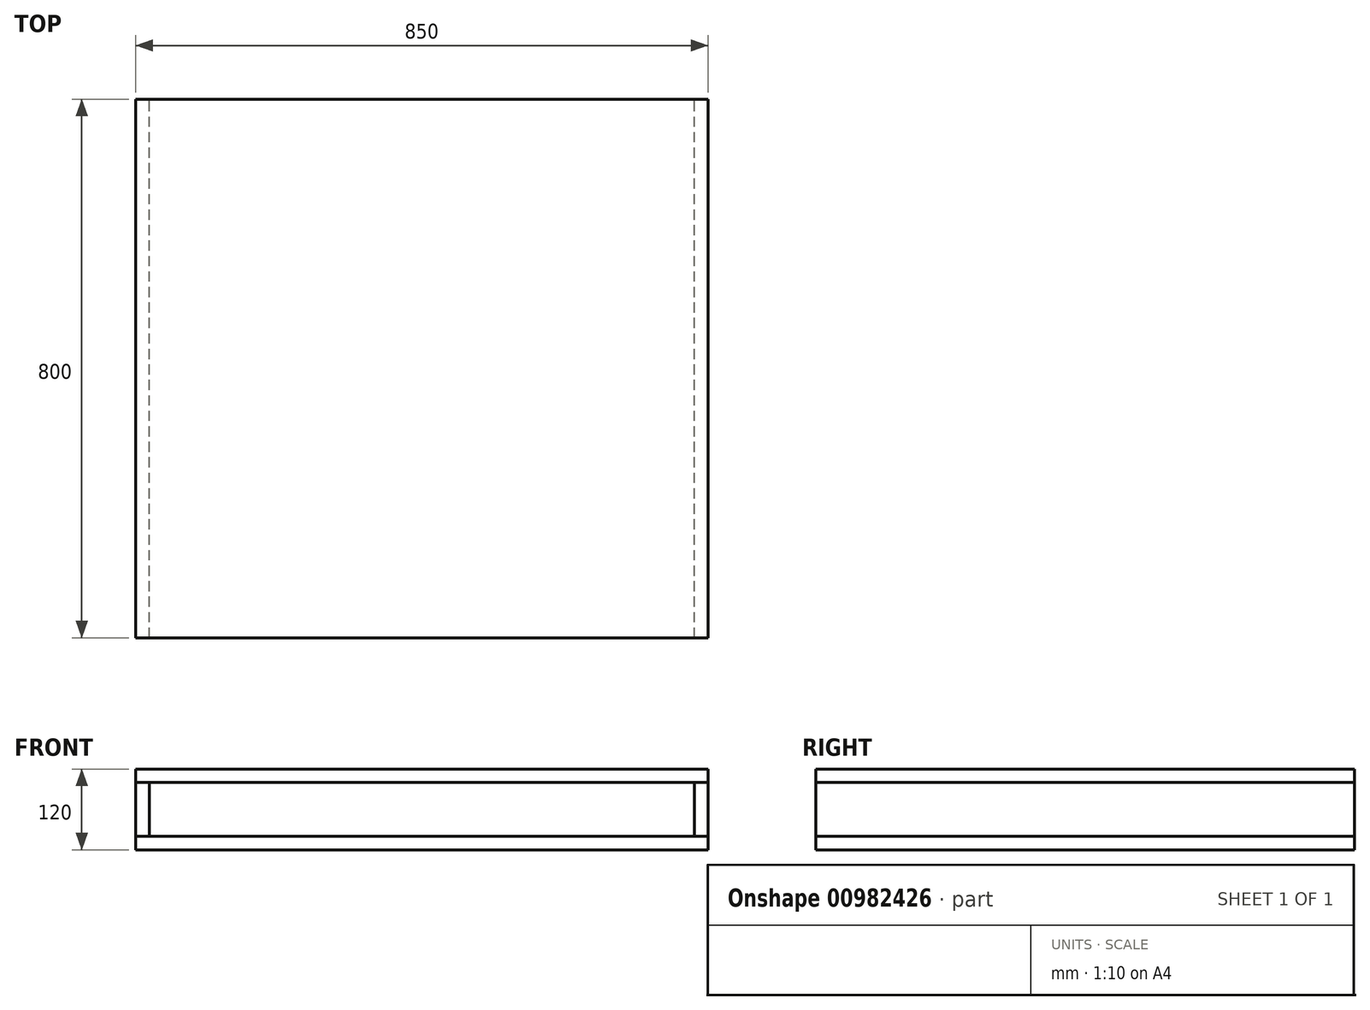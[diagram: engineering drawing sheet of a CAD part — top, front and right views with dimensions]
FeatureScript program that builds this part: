
annotation { "Feature Type Name" : "Feature", "Feature Type Description" : "" }
export const myFeature = defineFeature(function(context is Context, id is Id, definition is map)
    precondition{}
    {
        {
            var Q0;
            Q0=qCreatedBy(makeId("Front.planeOp"),FACE);
            var sketch = newSketch(context, id + "F0", { "sketchPlane" : qUnion([Q0])});
            skLineSegment(sketch, "E0.bottom", {"start": v(-425, 385) * mm, "end": v(425, 385) * mm});
            skLineSegment(sketch, "E0.top", {"start": v(-425, -385) * mm, "end": v(425, -385) * mm});
            skLineSegment(sketch, "E0.left", {"start": v(-425, 385) * mm, "end": v(-425, -385) * mm});
            skLineSegment(sketch, "E0.right", {"start": v(425, 385) * mm, "end": v(425, -385) * mm});
            skPoint(sketch, "E0.middle", {"position": v(0, 0) * mm});
            skLineSegment(sketch, "E1", {"start": v(-425, 365) * mm, "end": v(425, 365) * mm});
            skLineSegment(sketch, "E2", {"start": v(-425, 285) * mm, "end": v(425, 285) * mm});
            skLineSegment(sketch, "E3", {"start": v(-425, 265) * mm, "end": v(425, 265) * mm});
            skLineSegment(sketch, "E4", {"start": v(-405, 365) * mm, "end": v(-405, 285) * mm});
            skLineSegment(sketch, "E5", {"start": v(405, 365) * mm, "end": v(405, 285) * mm});
            skSolve(sketch);
        }
        {
            var Q0;
            {var subQ0=sQuery(id+"F0.wireOp",EDGE,"E0.bottom");Q0=makeQuery(id+"F0.imprint","IMPRINT",FACE,{"disambiguationData":[TD([[makeQuery(id+"F0.imprint","IMPRINT",EDGE,{"derivedFrom":subQ0}),-1.0]])]});}
            var Q1;
            {var subQ6=sQuery(id+"F0.wireOp",EDGE,"E3");Q1=makeQuery(id+"F0.imprint","IMPRINT",FACE,{"disambiguationData":[TD([[makeQuery(id+"F0.imprint","IMPRINT",EDGE,{"derivedFrom":subQ6}),1.0]])]});}
            extrude(context, id + "F1", {"entities" : qUnion([Q0, Q1]), "depth" : 800 * mm, "offsetDistance" : 25 * mm});
        }
        {
            var Q0;
            {var subQ5=sQuery(id+"F0.wireOp",EDGE,"E5");Q0=makeQuery(id+"F0.imprint","IMPRINT",FACE,{"disambiguationData":[TD([[makeQuery(id+"F0.imprint","IMPRINT",EDGE,{"derivedFrom":subQ5}),1.0]])]});}
            var Q1;
            {var subQ5=sQuery(id+"F0.wireOp",EDGE,"E4");Q1=makeQuery(id+"F0.imprint","IMPRINT",FACE,{"disambiguationData":[TD([[makeQuery(id+"F0.imprint","IMPRINT",EDGE,{"derivedFrom":subQ5}),-1.0]])]});}
            extrude(context, id + "F2", {"entities" : qUnion([Q0, Q1]), "depth" : 800 * mm, "offsetDistance" : 25 * mm});
        }
    });
